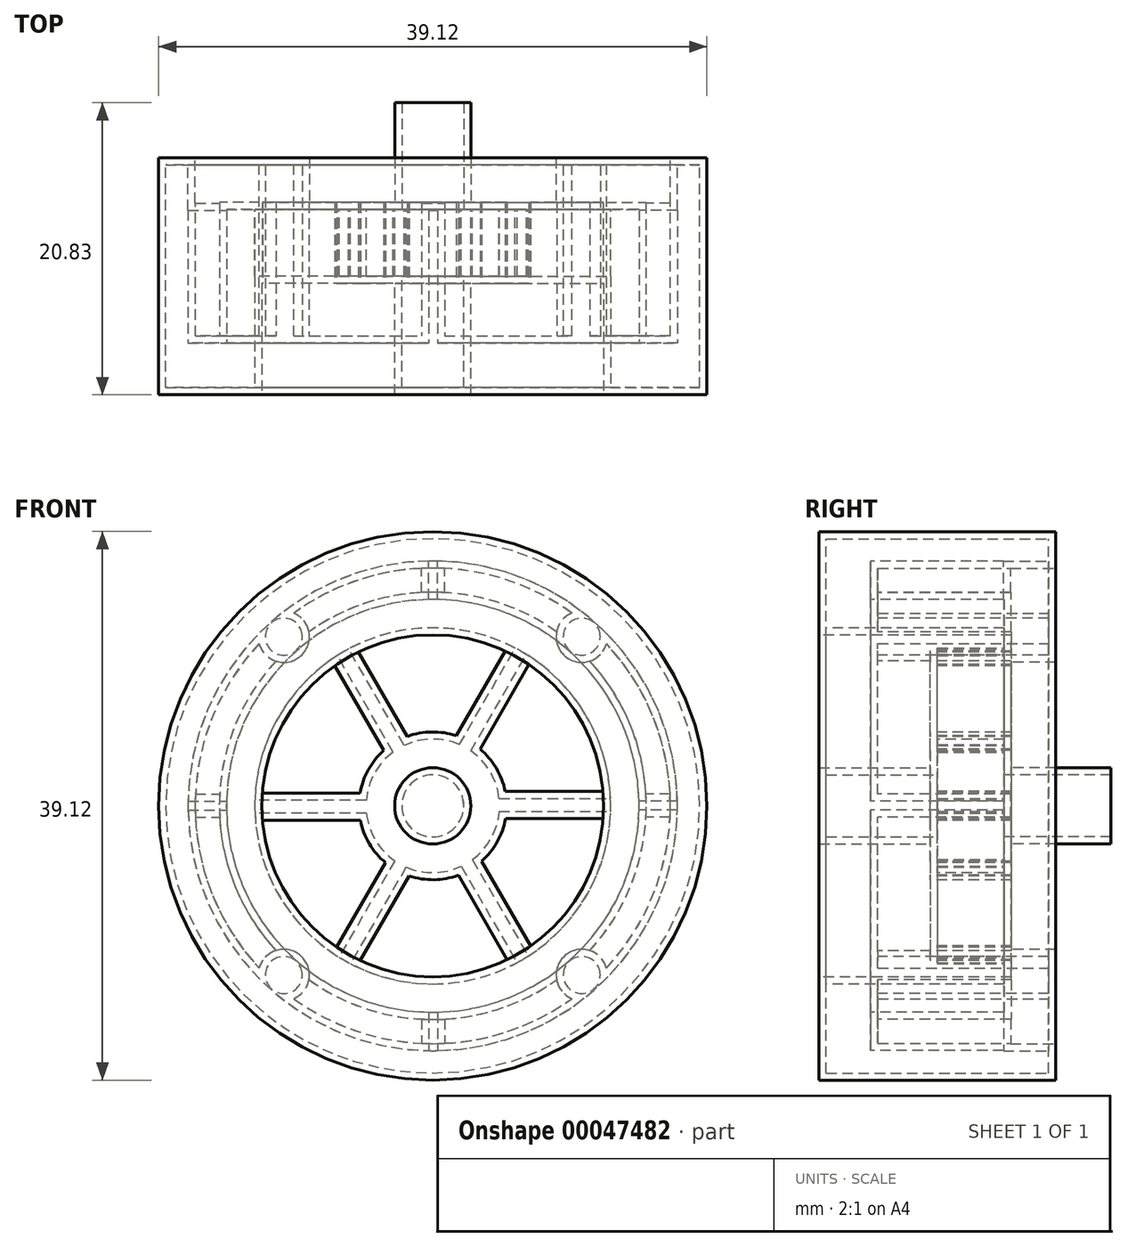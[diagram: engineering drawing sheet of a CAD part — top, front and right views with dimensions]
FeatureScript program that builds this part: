
annotation { "Feature Type Name" : "Feature", "Feature Type Description" : "" }
export const myFeature = defineFeature(function(context is Context, id is Id, definition is map)
    precondition{}
    {
        {
            var Q0;
            Q0=qCreatedBy(makeId("Front.planeOp"),FACE);
            var sketch = newSketch(context, id + "F0", { "sketchPlane" : qUnion([Q0])});
            skCircle(sketch, "E0", {"center": v(0, 0) * mm, "radius": 19.05 * mm});
            skSolve(sketch);
        }
        {
            var Q0;
            Q0 = qSketchRegion(id + "F0", true);
            extrude(context, id + "F1", {"entities" : qUnion([Q0]), "depth" : 15.88 * mm, "symmetric" : true});
        }
        {
            var Q0;
            Q0=makeQuery(id+"F1.opExtrude","CAP_FACE",FACE,{"disambiguationData":[OSD([sQuery(id+"F0.wireOp",EDGE,"E0")])],"isStart":true});
            var sketch = newSketch(context, id + "F2", { "sketchPlane" : qUnion([Q0])});
            skCircle(sketch, "E1", {"center": v(0, 0) * mm, "radius": 17.46 * mm});
            skSolve(sketch);
        }
        {
            var Q0;
            Q0 = qSketchRegion(id + "F2", true);
            extrude(context, id + "F3", {"entities" : qUnion([Q0]), "operationType" : NewBodyOperationType.REMOVE, "oppositeDirection" : true, "depth" : 12.7 * mm});
        }
        {
            var Q0;
            Q0=makeQuery(id+"F1.opExtrude","CAP_FACE",FACE,{"disambiguationData":[OSD([sQuery(id+"F0.wireOp",EDGE,"E0")])],"isStart":false});
            var sketch = newSketch(context, id + "F4", { "sketchPlane" : qUnion([Q0])});
            skCircle(sketch, "E2", {"center": v(0, 0) * mm, "radius": 12.7 * mm});
            skSolve(sketch);
        }
        {
            var Q0;
            Q0=makeQuery(id+"F4.imprint","IMPRINT",FACE,{"disambiguationData":[TD([[makeQuery(id+"F4.imprint","IMPRINT",EDGE,{"derivedFrom":sQuery(id+"F4.wireOp",EDGE,"E2")}),1.0]])]});
            extrude(context, id + "F5", {"entities" : qUnion([Q0]), "operationType" : NewBodyOperationType.REMOVE, "oppositeDirection" : true, "depth" : 12.7 * mm});
        }
        {
            var Q0;
            Q0=makeQuery(id+"F3.boolean.opBoolean","COPY",FACE,{"derivedFrom":makeQuery(id+"F3.opExtrude","CAP_FACE",FACE,{"disambiguationData":[OSD([sQuery(id+"F2.wireOp",EDGE,"E1")])],"isStart":false})});
            var sketch = newSketch(context, id + "F6", { "sketchPlane" : qUnion([Q0])});
            skCircle(sketch, "E3", {"center": v(0, 0) * mm, "radius": 12.7 * mm});
            skPoint(sketch, "E3.first.point", {"position": v(7.48, -10.27) * mm});
            skPoint(sketch, "E3.second.point", {"position": v(-7.74, -10.07) * mm});
            skPoint(sketch, "E3.third.point", {"position": v(-6.39, 10.98) * mm});
            skCircle(sketch, "E4", {"center": v(0, 0) * mm, "radius": 14.72 * mm});
            skSolve(sketch);
        }
        {
            var Q0;
            Q0 = qSketchRegion(id + "F6", true);
            extrude(context, id + "F7", {"entities" : qUnion([Q0]), "operationType" : NewBodyOperationType.ADD, "depth" : 9.52 * mm});
        }
        {
            var Q0;
            Q0=makeQuery(id+"F3.boolean.opBoolean","COPY",FACE,{"derivedFrom":makeQuery(id+"F3.opExtrude","CAP_FACE",FACE,{"disambiguationData":[OSD([sQuery(id+"F2.wireOp",EDGE,"E1")])],"isStart":false})});
            var sketch = newSketch(context, id + "F8", { "sketchPlane" : qUnion([Q0])});
            skArc(sketch, "E5", {"start": v(0.3, 17.46) * mm, "mid": v(-0.02, 17.46) * mm, "end": v(-0.33, 17.46) * mm});
            skLineSegment(sketch, "E6", {"start": v(-0.33, 14.72) * mm, "end": v(-0.33, 17.46) * mm});
            skLineSegment(sketch, "E7", {"start": v(0.3, 14.72) * mm, "end": v(0.3, 17.46) * mm});
            skArc(sketch, "E8.trimOffspring", {"start": v(0.3, 14.72) * mm, "mid": v(-0.02, 14.72) * mm, "end": v(-0.33, 14.72) * mm});
            skArc(sketch, "E9.MirrorCS", {"start": v(0.3, -17.46) * mm, "mid": v(-0.02, -17.46) * mm, "end": v(-0.33, -17.46) * mm});
            skLineSegment(sketch, "E10.MirrorCS", {"start": v(0.3, -14.72) * mm, "end": v(0.3, -17.46) * mm});
            skLineSegment(sketch, "E11.MirrorCS", {"start": v(-0.33, -14.72) * mm, "end": v(-0.33, -17.46) * mm});
            skArc(sketch, "E12.MirrorCS", {"start": v(0.3, -14.72) * mm, "mid": v(-0.02, -14.72) * mm, "end": v(-0.33, -14.72) * mm});
            skArc(sketch, "E13", {"start": v(-0.33, -14.72) * mm, "mid": v(-0.02, -14.72) * mm, "end": v(0.3, -14.72) * mm});
            skArc(sketch, "E14", {"start": v(-17.46, 0.32) * mm, "mid": v(-17.46, 0) * mm, "end": v(-17.46, -0.3) * mm});
            skLineSegment(sketch, "E15", {"start": v(-17.46, -0.3) * mm, "end": v(-14.72, -0.3) * mm});
            skLineSegment(sketch, "E16", {"start": v(-17.46, 0.32) * mm, "end": v(-14.72, 0.32) * mm});
            skArc(sketch, "E17.trimOffspring", {"start": v(-14.72, 0.32) * mm, "mid": v(-14.72, 0) * mm, "end": v(-14.72, -0.3) * mm});
            skArc(sketch, "E18.trimOffspring", {"start": v(-0.33, -17.46) * mm, "mid": v(-0.02, -17.46) * mm, "end": v(0.3, -17.46) * mm});
            skLineSegment(sketch, "E19.MirrorCS", {"start": v(17.46, 0.32) * mm, "end": v(14.72, 0.32) * mm});
            skLineSegment(sketch, "E20.MirrorCS", {"start": v(17.46, -0.3) * mm, "end": v(14.72, -0.3) * mm});
            skArc(sketch, "E21.MirrorCS", {"start": v(17.46, 0.32) * mm, "mid": v(17.46, 0) * mm, "end": v(17.46, -0.3) * mm});
            skArc(sketch, "E22.MirrorCS", {"start": v(14.72, 0.32) * mm, "mid": v(14.72, 0) * mm, "end": v(14.72, -0.3) * mm});
            skArc(sketch, "E23.trimOffspring", {"start": v(17.46, -0.3) * mm, "mid": v(17.46, 0) * mm, "end": v(17.46, 0.32) * mm});
            skArc(sketch, "E24.trimOffspring", {"start": v(14.72, -0.3) * mm, "mid": v(14.72, 0) * mm, "end": v(14.72, 0.32) * mm});
            skSolve(sketch);
        }
        {
            var Q0;
            Q0 = qSketchRegion(id + "F8", true);
            extrude(context, id + "F9", {"entities" : qUnion([Q0]), "operationType" : NewBodyOperationType.ADD, "depth" : 9.47 * mm});
        }
        {
            var Q0;
            {var subQ0=sQuery(id+"F2.wireOp",EDGE,"E1");Q0=makeQuery(id+"F9.boolean.opBoolean","SPLIT",FACE,{"disambiguationData":[TD([makeQuery(id+"F9.opExtrude","SWEPT_FACE",FACE,{"disambiguationData":[OSD([sQuery(id+"F8.wireOp",EDGE,"E11.MirrorCS")])]})])],"derivedFrom":makeQuery(id+"F3.boolean.opBoolean","COPY",FACE,{"derivedFrom":makeQuery(id+"F3.opExtrude","CAP_FACE",FACE,{"disambiguationData":[OSD([subQ0])],"isStart":false})})});}
            var sketch = newSketch(context, id + "F10", { "sketchPlane" : qUnion([Q0])});
            skCircle(sketch, "E25", {"center": v(-10.63, -12.06) * mm, "radius": 1.32 * mm});
            skCircle(sketch, "E26.MirrorC", {"center": v(-10.63, 12.06) * mm, "radius": 1.32 * mm});
            skCircle(sketch, "E27.MirrorC", {"center": v(10.63, 12.06) * mm, "radius": 1.32 * mm});
            skCircle(sketch, "E28.MirrorC", {"center": v(10.63, -12.06) * mm, "radius": 1.32 * mm});
            skSolve(sketch);
        }
        {
            var Q0;
            Q0 = qSketchRegion(id + "F10", true);
            extrude(context, id + "F11", {"entities" : qUnion([Q0]), "operationType" : NewBodyOperationType.ADD, "depth" : 12.7 * mm});
        }
        {
            var Q0;
            Q0=qCreatedBy(makeId("Front.planeOp"),FACE);
            var sketch = newSketch(context, id + "F12", { "sketchPlane" : qUnion([Q0])});
            skCircle(sketch, "E29", {"center": v(0, 0) * mm, "radius": 12.7 * mm});
            skSolve(sketch);
        }
        {
            var Q0;
            Q0 = qSketchRegion(id + "F12", true);
            var Q1;
            Q1=makeQuery(id+"F7.opExtrude","CAP_FACE",FACE,{"disambiguationData":[OSD([sQuery(id+"F6.wireOp",EDGE,"E3"),sQuery(id+"F6.wireOp",EDGE,"E4")])],"isStart":false});
            var Q2;
            Q2=makeQuery(id+"F7.opExtrude","CAP_FACE",FACE,{"disambiguationData":[OSD([sQuery(id+"F6.wireOp",EDGE,"E3"),sQuery(id+"F6.wireOp",EDGE,"E4")])],"isStart":false});
            extrude(context, id + "F13", {"entities" : qUnion([Q0]), "operationType" : NewBodyOperationType.ADD, "endBound" : BoundingType.UP_TO_SURFACE, "oppositeDirection" : true, "endBoundEntityFace" : qUnion([Q1]), "depth" : 3.17 * mm});
        }
        {
            var Q0;
            Q0=makeQuery(id+"F13.opExtrude","CAP_FACE",FACE,{"disambiguationData":[OSD([sQuery(id+"F12.wireOp",EDGE,"E29")])],"isStart":true});
            var sketch = newSketch(context, id + "F14", { "sketchPlane" : qUnion([Q0])});
            skCircle(sketch, "E30", {"center": v(0, 0) * mm, "radius": 4.76 * mm});
            skCircle(sketch, "E31", {"center": v(0, 0) * mm, "radius": 12.7 * mm});
            skPoint(sketch, "E31.first.point", {"position": v(-10.34, 7.37) * mm});
            skPoint(sketch, "E31.second.point", {"position": v(9.04, 8.92) * mm});
            skPoint(sketch, "E31.third.point", {"position": v(11.08, 6.21) * mm});
            skSolve(sketch);
        }
        {
            var Q0;
            Q0=makeQuery(id+"F14.imprint","IMPRINT",FACE,{"disambiguationData":[TD([[makeQuery(id+"F14.imprint","IMPRINT",EDGE,{"derivedFrom":sQuery(id+"F14.wireOp",EDGE,"E30")}),-1.0]])]});
            extrude(context, id + "F15", {"entities" : qUnion([Q0]), "operationType" : NewBodyOperationType.REMOVE, "endBound" : BoundingType.THROUGH_ALL, "oppositeDirection" : true, "depth" : 25.4 * mm});
        }
        {
            var Q0;
            {var subQ0=sQuery(id+"F6.wireOp",EDGE,"E4");var subQ1=sQuery(id+"F6.wireOp",EDGE,"E3");Q0=makeQuery(id+"F15.boolean.opBoolean","SPLIT",FACE,{"disambiguationData":[TD([makeQuery(id+"F15.opExtrude","SWEPT_FACE",FACE,{"disambiguationData":[OSD([sQuery(id+"F14.wireOp",EDGE,"E30")])]})])],"derivedFrom":makeQuery(id+"F13.boolean.opBoolean","MERGE",FACE,{"derivedFrom":[makeQuery(id+"F7.opExtrude","CAP_FACE",FACE,{"disambiguationData":[OSD([subQ1,subQ0])],"isStart":false}),makeQuery(id+"F13.opExtrude","CAP_FACE",FACE,{"disambiguationData":[OSD([subQ1,subQ0])],"isStart":false})]})});}
            var sketch = newSketch(context, id + "F16", { "sketchPlane" : qUnion([Q0])});
            skLineSegment(sketch, "E32", {"start": v(-4.73, 0.54) * mm, "end": v(-12.69, 0.54) * mm});
            skLineSegment(sketch, "E33", {"start": v(-4.75, -0.39) * mm, "end": v(-12.7, -0.39) * mm});
            skArc(sketch, "E34", {"start": v(-4.73, 0.54) * mm, "mid": v(-4.76, 0.07) * mm, "end": v(-4.75, -0.39) * mm});
            skArc(sketch, "E35", {"start": v(-12.69, 0.54) * mm, "mid": v(-12.7, 0.07) * mm, "end": v(-12.7, -0.39) * mm});
            skSolve(sketch);
        }
        {
            var Q0;
            Q0=makeQuery(id+"F16.imprint","IMPRINT",FACE,{"disambiguationData":[TD([[makeQuery(id+"F16.imprint","IMPRINT",EDGE,{"derivedFrom":sQuery(id+"F16.wireOp",EDGE,"E32")}),1.0]])]});
            var Q1;
            Q1=makeQuery(id+"F13.opExtrude","CAP_FACE",FACE,{"disambiguationData":[OSD([sQuery(id+"F12.wireOp",EDGE,"E29")])],"isStart":true});
            extrude(context, id + "F17", {"entities" : qUnion([Q0]), "endBound" : BoundingType.UP_TO_SURFACE, "oppositeDirection" : true, "endBoundEntityFace" : qUnion([Q1]), "depth" : 25.4 * mm});
        }
        {
            var Q0;
            Q0=makeQuery(id+"F17.opExtrude","SWEPT_BODY",BODY,{"disambiguationData":[OSD([sQuery(id+"F16.wireOp",EDGE,"E32"),sQuery(id+"F16.wireOp",EDGE,"E33"),sQuery(id+"F16.wireOp",EDGE,"E34"),sQuery(id+"F16.wireOp",EDGE,"E35")])]});
            var Q1;
            {var subQ0=sQuery(id+"F6.wireOp",EDGE,"E4");var subQ1=sQuery(id+"F6.wireOp",EDGE,"E3");Q1=makeQuery(id+"F15.boolean.opBoolean","INTERSECT",EDGE,{"derivedFrom":[makeQuery(id+"F13.boolean.opBoolean","MERGE",FACE,{"derivedFrom":[makeQuery(id+"F7.opExtrude","CAP_FACE",FACE,{"disambiguationData":[OSD([subQ1,subQ0])],"isStart":false}),makeQuery(id+"F13.opExtrude","CAP_FACE",FACE,{"disambiguationData":[OSD([subQ1,subQ0])],"isStart":false})]}),makeQuery(id+"F15.opExtrude","SWEPT_FACE",FACE,{"disambiguationData":[OSD([sQuery(id+"F14.wireOp",EDGE,"E31")])]})]});}
            circularPattern(context, id + "F18", {"entities" : qUnion([Q0]), "axis" : qUnion([Q1]), "angle" : 360 * degree, "instanceCount" : 6, "equalSpace" : true});
        }
        {
            var Q0;
            Q0=makeQuery(id+"F15.boolean.opBoolean","SPLIT",BODY,{"disambiguationData":[OD(0.0)],"derivedFrom":makeQuery(id+"F1.opExtrude","SWEPT_BODY",BODY,{"disambiguationData":[OSD([sQuery(id+"F0.wireOp",EDGE,"E0")])]})});
            var Q1;
            Q1=makeQuery(id+"F15.boolean.opBoolean","SPLIT",BODY,{"disambiguationData":[OD(1.0)],"derivedFrom":makeQuery(id+"F1.opExtrude","SWEPT_BODY",BODY,{"disambiguationData":[OSD([sQuery(id+"F0.wireOp",EDGE,"E0")])]})});
            var Q2;
            Q2=makeQuery(id+"F17.opExtrude","SWEPT_BODY",BODY,{"disambiguationData":[OSD([sQuery(id+"F16.wireOp",EDGE,"E32"),sQuery(id+"F16.wireOp",EDGE,"E33"),sQuery(id+"F16.wireOp",EDGE,"E34"),sQuery(id+"F16.wireOp",EDGE,"E35")])]});
            var Q3;
            Q3=makeQuery(id+"F18.opPattern","COPY",BODY,{"derivedFrom":makeQuery(id+"F17.opExtrude","SWEPT_BODY",BODY,{"disambiguationData":[OSD([sQuery(id+"F16.wireOp",EDGE,"E32"),sQuery(id+"F16.wireOp",EDGE,"E33"),sQuery(id+"F16.wireOp",EDGE,"E34"),sQuery(id+"F16.wireOp",EDGE,"E35")])]}),"instanceName":"1"});
            var Q4;
            Q4=makeQuery(id+"F18.opPattern","COPY",BODY,{"derivedFrom":makeQuery(id+"F17.opExtrude","SWEPT_BODY",BODY,{"disambiguationData":[OSD([sQuery(id+"F16.wireOp",EDGE,"E32"),sQuery(id+"F16.wireOp",EDGE,"E33"),sQuery(id+"F16.wireOp",EDGE,"E34"),sQuery(id+"F16.wireOp",EDGE,"E35")])]}),"instanceName":"2"});
            var Q5;
            Q5=makeQuery(id+"F18.opPattern","COPY",BODY,{"derivedFrom":makeQuery(id+"F17.opExtrude","SWEPT_BODY",BODY,{"disambiguationData":[OSD([sQuery(id+"F16.wireOp",EDGE,"E32"),sQuery(id+"F16.wireOp",EDGE,"E33"),sQuery(id+"F16.wireOp",EDGE,"E34"),sQuery(id+"F16.wireOp",EDGE,"E35")])]}),"instanceName":"3"});
            booleanBodies(context, id + "F19", {"operationType" : BooleanOperationType.UNION, "tools" : qUnion([Q0, Q1, Q2, Q3, Q4, Q5])});
        }
        {
            var Q0;
            Q0=makeQuery(id+"F15.boolean.opBoolean","SPLIT",BODY,{"disambiguationData":[OD(0.0)],"derivedFrom":makeQuery(id+"F1.opExtrude","SWEPT_BODY",BODY,{"disambiguationData":[OSD([sQuery(id+"F0.wireOp",EDGE,"E0")])]})});
            var Q1;
            Q1=makeQuery(id+"F18.opPattern","COPY",BODY,{"derivedFrom":makeQuery(id+"F17.opExtrude","SWEPT_BODY",BODY,{"disambiguationData":[OSD([sQuery(id+"F16.wireOp",EDGE,"E32"),sQuery(id+"F16.wireOp",EDGE,"E33"),sQuery(id+"F16.wireOp",EDGE,"E34"),sQuery(id+"F16.wireOp",EDGE,"E35")])]}),"instanceName":"4"});
            var Q2;
            Q2=makeQuery(id+"F18.opPattern","COPY",BODY,{"derivedFrom":makeQuery(id+"F17.opExtrude","SWEPT_BODY",BODY,{"disambiguationData":[OSD([sQuery(id+"F16.wireOp",EDGE,"E32"),sQuery(id+"F16.wireOp",EDGE,"E33"),sQuery(id+"F16.wireOp",EDGE,"E34"),sQuery(id+"F16.wireOp",EDGE,"E35")])]}),"instanceName":"5"});
            booleanBodies(context, id + "F20", {"operationType" : BooleanOperationType.UNION, "tools" : qUnion([Q0, Q1, Q2])});
        }
        {
            var Q0;
            {var subQ0=sQuery(id+"F12.wireOp",EDGE,"E29");var subQ1=makeQuery(id+"F17.opExtrude","CAP_FACE",FACE,{"disambiguationData":[OSD([subQ0])],"isStart":false});Q0=makeQuery(id+"F20.opBoolean","MERGE",FACE,{"derivedFrom":[makeQuery(id+"F18.opPattern","COPY",FACE,{"derivedFrom":subQ1,"instanceName":"4"}),makeQuery(id+"F18.opPattern","COPY",FACE,{"derivedFrom":subQ1,"instanceName":"5"}),makeQuery(id+"F19.opBoolean","MERGE",FACE,{"derivedFrom":[makeQuery(id+"F13.opExtrude","CAP_FACE",FACE,{"disambiguationData":[OSD([subQ0])],"isStart":true}),subQ1,makeQuery(id+"F18.opPattern","COPY",FACE,{"derivedFrom":subQ1,"instanceName":"1"}),makeQuery(id+"F18.opPattern","COPY",FACE,{"derivedFrom":subQ1,"instanceName":"2"}),makeQuery(id+"F18.opPattern","COPY",FACE,{"derivedFrom":subQ1,"instanceName":"3"})]})]});}
            var sketch = newSketch(context, id + "F21", { "sketchPlane" : qUnion([Q0])});
            skCircle(sketch, "E36", {"center": v(0, 0) * mm, "radius": 2.21 * mm});
            skSolve(sketch);
        }
        {
            var Q0;
            Q0 = qSketchRegion(id + "F21", true);
            var Q1;
            Q1=makeQuery(id+"F1.opExtrude","CAP_FACE",FACE,{"disambiguationData":[OSD([sQuery(id+"F0.wireOp",EDGE,"E0")])],"isStart":false});
            extrude(context, id + "F22", {"entities" : qUnion([Q0]), "operationType" : NewBodyOperationType.ADD, "endBound" : BoundingType.UP_TO_SURFACE, "endBoundEntityFace" : qUnion([Q1]), "depth" : 25.4 * mm});
        }
        {
            var Q0;
            {var subQ0=makeQuery(id+"F17.opExtrude","CAP_FACE",FACE,{"disambiguationData":[OSD([sQuery(id+"F16.wireOp",EDGE,"E32"),sQuery(id+"F16.wireOp",EDGE,"E33"),sQuery(id+"F16.wireOp",EDGE,"E34"),sQuery(id+"F16.wireOp",EDGE,"E35")])],"isStart":true});var subQ1=sQuery(id+"F6.wireOp",EDGE,"E3");var subQ2=sQuery(id+"F6.wireOp",EDGE,"E4");var subQ3=makeQuery(id+"F13.boolean.opBoolean","MERGE",FACE,{"derivedFrom":[makeQuery(id+"F7.opExtrude","CAP_FACE",FACE,{"disambiguationData":[OSD([subQ1,subQ2])],"isStart":false}),makeQuery(id+"F13.opExtrude","CAP_FACE",FACE,{"disambiguationData":[OSD([subQ1,subQ2])],"isStart":false})]});Q0=makeQuery(id+"F20.opBoolean","MERGE",FACE,{"derivedFrom":[makeQuery(id+"F18.opPattern","COPY",FACE,{"derivedFrom":subQ0,"instanceName":"4"}),makeQuery(id+"F18.opPattern","COPY",FACE,{"derivedFrom":subQ0,"instanceName":"5"}),makeQuery(id+"F19.opBoolean","MERGE",FACE,{"derivedFrom":[makeQuery(id+"F15.boolean.opBoolean","SPLIT",FACE,{"disambiguationData":[TD([makeQuery(id+"F15.opExtrude","SWEPT_FACE",FACE,{"disambiguationData":[OSD([sQuery(id+"F14.wireOp",EDGE,"E30")])]})])],"derivedFrom":subQ3}),makeQuery(id+"F15.boolean.opBoolean","SPLIT",FACE,{"disambiguationData":[TD([makeQuery(id+"F5.boolean.opBoolean","COPY",FACE,{"derivedFrom":makeQuery(id+"F5.opExtrude","SWEPT_FACE",FACE,{"disambiguationData":[OSD([sQuery(id+"F4.wireOp",EDGE,"E2")])]})})])],"derivedFrom":subQ3}),subQ0,makeQuery(id+"F18.opPattern","COPY",FACE,{"derivedFrom":subQ0,"instanceName":"1"}),makeQuery(id+"F18.opPattern","COPY",FACE,{"derivedFrom":subQ0,"instanceName":"2"}),makeQuery(id+"F18.opPattern","COPY",FACE,{"derivedFrom":subQ0,"instanceName":"3"})]})]});}
            var sketch = newSketch(context, id + "F23", { "sketchPlane" : qUnion([Q0])});
            skCircle(sketch, "E37", {"center": v(0, 0) * mm, "radius": 2.2 * mm});
            skSolve(sketch);
        }
        {
            var Q0;
            Q0=makeQuery(id+"F23.imprint","IMPRINT",FACE,{"disambiguationData":[TD([[makeQuery(id+"F23.imprint","IMPRINT",EDGE,{"derivedFrom":sQuery(id+"F23.wireOp",EDGE,"E37")}),1.0]])]});
            var Q1;
            Q1=sQuery(id+"F23.wireOp",EDGE,"E37");
            extrude(context, id + "F24", {"entities" : qUnion([Q0]), "operationType" : NewBodyOperationType.ADD, "surfaceEntities" : qUnion([Q1]), "depth" : 7.62 * mm});
        }
        {
            var Q0;
            Q0=makeQuery(id+"F24.opExtrude","CAP_FACE",FACE,{"disambiguationData":[OSD([sQuery(id+"F23.wireOp",EDGE,"E37")])],"isStart":false});
            shell(context, id + "F25", {"entities" : qUnion([Q0]), "thickness" : 0.5 * mm, "oppositeDirection" : true});
        }
    });
